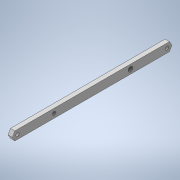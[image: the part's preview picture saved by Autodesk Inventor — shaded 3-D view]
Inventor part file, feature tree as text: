
AUTODESK INVENTOR PART (.ipt)
format: ipt  version: 2020 (Build 240168000, 168)  size: 195,072 bytes
history: native  units: in
note: dims shown in document units (in); Inventor stores cm internally (conversion verified against a paired STEP export)
features: extrude x4, sketch x4, other x3, projected_geometry x2
ambient origin geometry x8: Origin, YZ Plane, XZ Plane, XY Plane, X Axis, Y Axis, Z Axis, Center Point
bodies: Solid1 (feature_tree)
feature tree (13):
  other  "HexWheelGuard.ipt"
  extrude  "Extrusion1"  TaperAngle=0.0deg  [1 undecoded]
  extrude  "Extrusion2"  Depth=0.3937in
  extrude  "Extrusion3"  Depth=0.3937in TaperAngle=0.0deg
  extrude  "Extrusion4"  Depth=0.3937in TaperAngle=0.0deg
  other  "Solid1::HexWheelGuard.ipt"
  other  "TaggingFeature1"
  sketch  "Sketch1"  dims[d0=0.3937in d1=0.0in d2=0.0in]
  projected_geometry  "Projected Loop1"
  sketch  "Sketch2"  dims[d3=0.3937in d4=0.0in d5=0.122in]
  sketch  "Sketch3"  dims[d6=0.122in d7=0.3937in d8=0.0in]
  sketch  "Sketch4"  dims[d9=0.1575in d10=0.3937in d11=0.0in]
  projected_geometry  "Projected Loop2"
note: 1 required parameter value undecoded (feature->parameter linkage not recoverable at this tier; creation-order binding heuristic only, values carry confidence <= 0.55)
